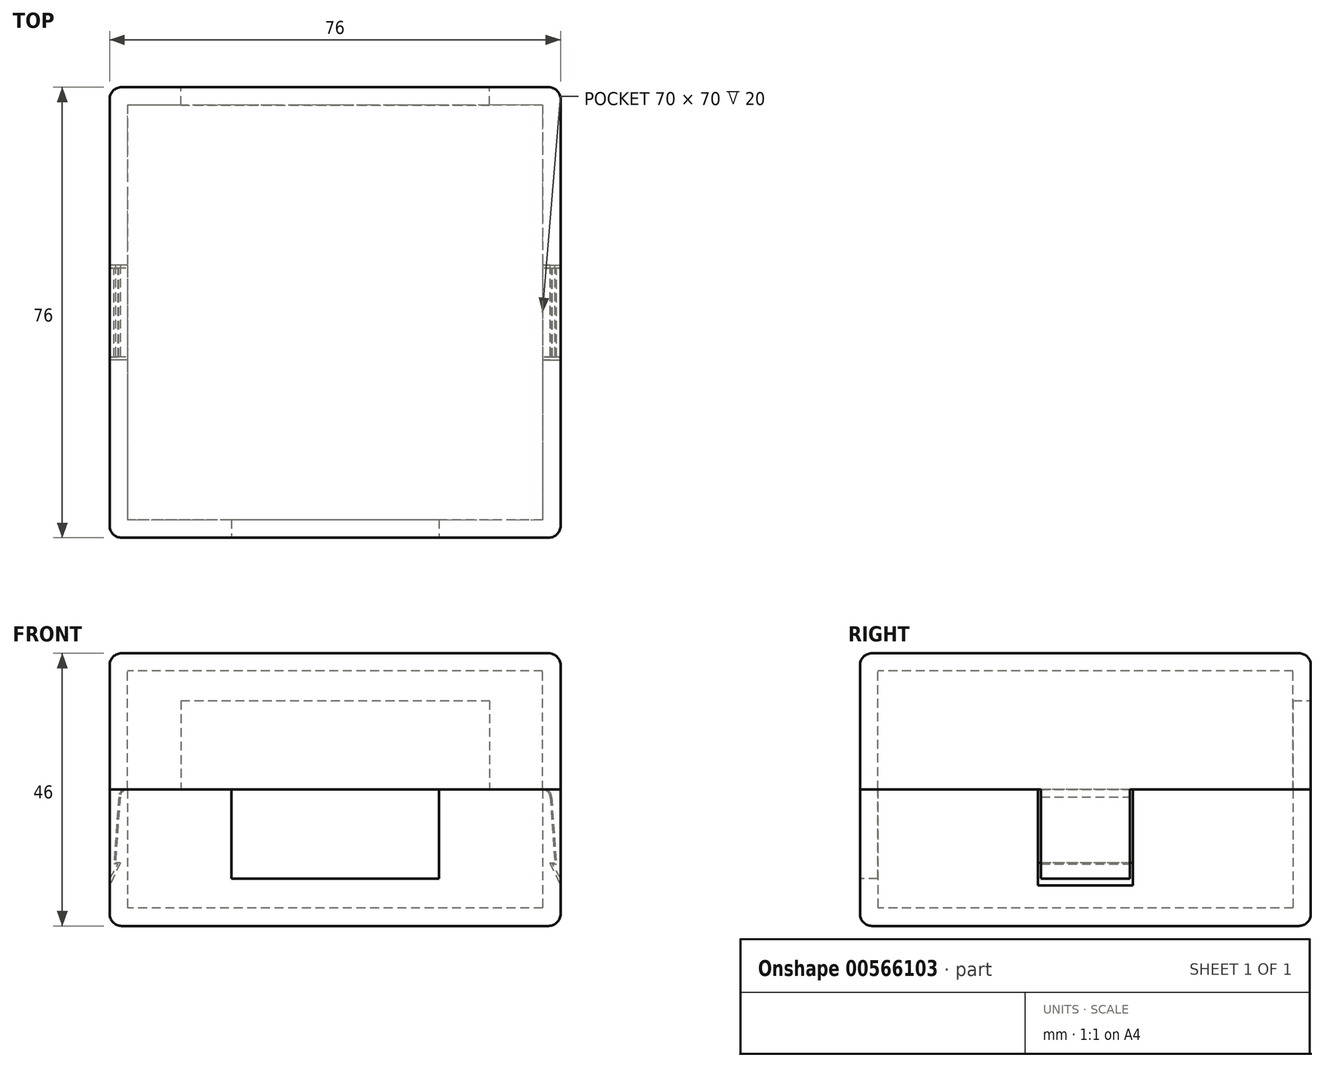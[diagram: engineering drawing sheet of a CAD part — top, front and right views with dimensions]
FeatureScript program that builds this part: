
annotation { "Feature Type Name" : "Feature", "Feature Type Description" : "" }
export const myFeature = defineFeature(function(context is Context, id is Id, definition is map)
    precondition{}
    {
        {
            var Q0;
            Q0=qCreatedBy(makeId("Top.planeOp"),FACE);
            var sketch = newSketch(context, id + "F0", { "sketchPlane" : qUnion([Q0])});
            skLineSegment(sketch, "E0.bottom", {"start": v(35, 35) * mm, "end": v(-35, 35) * mm});
            skLineSegment(sketch, "E0.top", {"start": v(35, -35) * mm, "end": v(-35, -35) * mm});
            skLineSegment(sketch, "E0.left", {"start": v(35, 35) * mm, "end": v(35, -35) * mm});
            skLineSegment(sketch, "E0.right", {"start": v(-35, 35) * mm, "end": v(-35, -35) * mm});
            skPoint(sketch, "E0.middle", {"position": v(0, 0) * mm});
            skLineSegment(sketch, "E1.0", {"start": v(38, 38) * mm, "end": v(-38, 38) * mm});
            skLineSegment(sketch, "E1.1", {"start": v(38, 38) * mm, "end": v(38, -38) * mm});
            skLineSegment(sketch, "E1.2", {"start": v(38, -38) * mm, "end": v(-38, -38) * mm});
            skLineSegment(sketch, "E1.3", {"start": v(-38, 38) * mm, "end": v(-38, -38) * mm});
            skSolve(sketch);
        }
        {
            var Q0;
            Q0=makeQuery(id+"F0.imprint","IMPRINT",FACE,{"disambiguationData":[TD([[makeQuery(id+"F0.imprint","IMPRINT",EDGE,{"derivedFrom":sQuery(id+"F0.wireOp",EDGE,"E0.bottom")}),-1.0]])]});
            var Q1;
            Q1=makeQuery(id+"F0.imprint","IMPRINT",FACE,{"disambiguationData":[TD([[makeQuery(id+"F0.imprint","IMPRINT",EDGE,{"derivedFrom":sQuery(id+"F0.wireOp",EDGE,"E0.bottom")}),1.0]])]});
            extrude(context, id + "F1", {"entities" : qUnion([Q0, Q1]), "oppositeDirection" : true, "depth" : 3 * mm, "offsetDistance" : 25 * mm});
        }
        {
            var Q0;
            Q0=makeQuery(id+"F0.imprint","IMPRINT",FACE,{"disambiguationData":[TD([[makeQuery(id+"F0.imprint","IMPRINT",EDGE,{"derivedFrom":sQuery(id+"F0.wireOp",EDGE,"E0.bottom")}),-1.0]])]});
            extrude(context, id + "F2", {"entities" : qUnion([Q0]), "operationType" : NewBodyOperationType.ADD, "depth" : 20 * mm, "offsetDistance" : 25 * mm});
        }
        {
            var Q0;
            Q0=makeQuery(id+"F1.opExtrude","SWEPT_BODY",BODY,{"disambiguationData":[OSD([sQuery(id+"F0.wireOp",EDGE,"E1.0"),sQuery(id+"F0.wireOp",EDGE,"E1.1"),sQuery(id+"F0.wireOp",EDGE,"E1.2"),sQuery(id+"F0.wireOp",EDGE,"E1.3")])]});
            var Q1;
            Q1=makeQuery(id+"F2.opExtrude","CAP_FACE",FACE,{"disambiguationData":[OSD([sQuery(id+"F0.wireOp",EDGE,"E0.bottom"),sQuery(id+"F0.wireOp",EDGE,"E0.top"),sQuery(id+"F0.wireOp",EDGE,"E0.left"),sQuery(id+"F0.wireOp",EDGE,"E0.right"),sQuery(id+"F0.wireOp",EDGE,"E1.0"),sQuery(id+"F0.wireOp",EDGE,"E1.1"),sQuery(id+"F0.wireOp",EDGE,"E1.2"),sQuery(id+"F0.wireOp",EDGE,"E1.3")])],"isStart":false});
            mirror(context, id + "F3", {"entities" : qUnion([Q0]), "mirrorPlane" : qUnion([Q1])});
        }
        {
            var Q0;
            {var subQ0=sQuery(id+"F0.wireOp",EDGE,"E1.2");Q0=makeQuery(id+"F3.opPattern","COPY",FACE,{"derivedFrom":makeQuery(id+"F2.boolean.opBoolean","MERGE",FACE,{"derivedFrom":[makeQuery(id+"F1.opExtrude","SWEPT_FACE",FACE,{"disambiguationData":[OSD([subQ0])]}),makeQuery(id+"F2.opExtrude","SWEPT_FACE",FACE,{"disambiguationData":[OSD([subQ0])]})]}),"instanceName":"1"});}
            var sketch = newSketch(context, id + "F4", { "sketchPlane" : qUnion([Q0])});
            skLineSegment(sketch, "E2.bottom", {"start": v(-17.5, 20) * mm, "end": v(17.5, 20) * mm});
            skLineSegment(sketch, "E2.top", {"start": v(-17.5, 5) * mm, "end": v(17.5, 5) * mm});
            skLineSegment(sketch, "E2.left", {"start": v(-17.5, 20) * mm, "end": v(-17.5, 5) * mm});
            skLineSegment(sketch, "E2.right", {"start": v(17.5, 20) * mm, "end": v(17.5, 5) * mm});
            skPoint(sketch, "E2.middle", {"position": v(0, 12.5) * mm});
            skSolve(sketch);
        }
        {
            var Q0;
            Q0=makeQuery(id+"F4.imprint","IMPRINT",FACE,{"disambiguationData":[TD([[makeQuery(id+"F4.imprint","IMPRINT",EDGE,{"derivedFrom":sQuery(id+"F4.wireOp",EDGE,"E2.bottom")}),1.0]])]});
            extrude(context, id + "F5", {"entities" : qUnion([Q0]), "operationType" : NewBodyOperationType.REMOVE, "endBound" : BoundingType.UP_TO_NEXT, "oppositeDirection" : true, "depth" : 25 * mm, "offsetDistance" : 25 * mm});
        }
        {
            var Q0;
            {var subQ0=sQuery(id+"F0.wireOp",EDGE,"E1.0");Q0=makeQuery(id+"F3.opPattern","COPY",FACE,{"derivedFrom":makeQuery(id+"F2.boolean.opBoolean","MERGE",FACE,{"derivedFrom":[makeQuery(id+"F1.opExtrude","SWEPT_FACE",FACE,{"disambiguationData":[OSD([subQ0])]}),makeQuery(id+"F2.opExtrude","SWEPT_FACE",FACE,{"disambiguationData":[OSD([subQ0])]})]}),"instanceName":"1"});}
            var sketch = newSketch(context, id + "F6", { "sketchPlane" : qUnion([Q0])});
            skLineSegment(sketch, "E3.bottom", {"start": v(26, 35) * mm, "end": v(-26, 35) * mm});
            skLineSegment(sketch, "E3.top", {"start": v(26, 20) * mm, "end": v(-26, 20) * mm});
            skLineSegment(sketch, "E3.left", {"start": v(26, 35) * mm, "end": v(26, 20) * mm});
            skLineSegment(sketch, "E3.right", {"start": v(-26, 35) * mm, "end": v(-26, 20) * mm});
            skPoint(sketch, "E3.middle", {"position": v(0, 27.5) * mm});
            skSolve(sketch);
        }
        {
            var Q0;
            Q0=makeQuery(id+"F6.imprint","IMPRINT",FACE,{"disambiguationData":[TD([[makeQuery(id+"F6.imprint","IMPRINT",EDGE,{"derivedFrom":sQuery(id+"F6.wireOp",EDGE,"E3.bottom")}),1.0]])]});
            extrude(context, id + "F7", {"entities" : qUnion([Q0]), "operationType" : NewBodyOperationType.REMOVE, "endBound" : BoundingType.UP_TO_NEXT, "oppositeDirection" : true, "depth" : 25 * mm, "offsetDistance" : 25 * mm});
        }
        {
            var Q0;
            Q0=qCreatedBy(makeId("Front.planeOp"),FACE);
            var sketch = newSketch(context, id + "F8", { "sketchPlane" : qUnion([Q0])});
            skLineSegment(sketch, "E4.0", {"start": v(38, 43) * mm, "end": v(38, 20) * mm});
            skLineSegment(sketch, "E5", {"start": v(38, 20) * mm, "end": v(38, 5) * mm});
            skLineSegment(sketch, "E6", {"start": v(38, 5) * mm, "end": v(36.6, 7.42) * mm});
            skLineSegment(sketch, "E7", {"start": v(36.6, 7.42) * mm, "end": v(37.3, 7.42) * mm});
            skLineSegment(sketch, "E8", {"start": v(36.4, 20) * mm, "end": v(38, 20) * mm});
            skLineSegment(sketch, "E9.0", {"start": v(38, 20) * mm, "end": v(-38, 20) * mm});
            skArc(sketch, "E10", {"start": v(36.49, 18.76) * mm, "mid": v(36.13, 19.64) * mm, "end": v(35.25, 20) * mm});
            skLineSegment(sketch, "E11", {"start": v(35.25, 20) * mm, "end": v(36.4, 20) * mm});
            skLineSegment(sketch, "E12", {"start": v(36.49, 18.76) * mm, "end": v(37.3, 7.42) * mm});
            skLineSegment(sketch, "E13", {"start": v(36.49, 18.76) * mm, "end": v(36.4, 20) * mm, "construction": true});
            skLineSegment(sketch, "E14.0", {"start": v(36.24, 18.76) * mm, "end": v(37.03, 7.67) * mm});
            skLineSegment(sketch, "E14.1", {"start": v(36.2, 7.67) * mm, "end": v(37.03, 7.67) * mm});
            skArc(sketch, "E15", {"start": v(36.24, 18.76) * mm, "mid": v(35.85, 19.61) * mm, "end": v(35, 20) * mm});
            skLineSegment(sketch, "E16", {"start": v(36.2, 7.67) * mm, "end": v(38, 3.81) * mm});
            skLineSegment(sketch, "E17.MirrorCS", {"start": v(-36.6, 7.42) * mm, "end": v(-37.3, 7.42) * mm});
            skLineSegment(sketch, "E18.MirrorCS", {"start": v(-38, 5) * mm, "end": v(-36.6, 7.42) * mm});
            skLineSegment(sketch, "E19.MirrorCS", {"start": v(-36.2, 7.67) * mm, "end": v(-38, 3.81) * mm});
            skLineSegment(sketch, "E20.MirrorCS", {"start": v(-36.2, 7.67) * mm, "end": v(-37.03, 7.67) * mm});
            skLineSegment(sketch, "E21.MirrorCS", {"start": v(-36.24, 18.76) * mm, "end": v(-37.03, 7.67) * mm});
            skLineSegment(sketch, "E22.MirrorCS", {"start": v(-36.49, 18.76) * mm, "end": v(-37.3, 7.42) * mm});
            skArc(sketch, "E23.MirrorCS", {"start": v(-36.49, 18.76) * mm, "mid": v(-36.13, 19.64) * mm, "end": v(-35.25, 20) * mm});
            skArc(sketch, "E24.MirrorCS", {"start": v(-36.24, 18.76) * mm, "mid": v(-35.85, 19.61) * mm, "end": v(-35, 20) * mm});
            skLineSegment(sketch, "E25", {"start": v(-38, 20) * mm, "end": v(-38, 3.81) * mm});
            skLineSegment(sketch, "E26", {"start": v(38, 5) * mm, "end": v(38, 3.81) * mm});
            skSolve(sketch);
        }
        {
            var Q0;
            Q0=makeQuery(id+"F8.imprint","IMPRINT",FACE,{"disambiguationData":[TD([[makeQuery(id+"F8.imprint","IMPRINT",EDGE,{"derivedFrom":sQuery(id+"F8.wireOp",EDGE,"E17.MirrorCS")}),-1.0]])]});
            var Q1;
            Q1=makeQuery(id+"F8.imprint","IMPRINT",FACE,{"disambiguationData":[TD([[makeQuery(id+"F8.imprint","IMPRINT",EDGE,{"derivedFrom":sQuery(id+"F8.wireOp",EDGE,"E17.MirrorCS")}),1.0]])]});
            var Q2;
            {var subQ1=sQuery(id+"F8.wireOp",EDGE,"E5");Q2=makeQuery(id+"F8.imprint","IMPRINT",FACE,{"disambiguationData":[TD([[makeQuery(id+"F8.imprint","IMPRINT",EDGE,{"derivedFrom":subQ1}),-1.0]])]});}
            var Q3;
            Q3=makeQuery(id+"F8.imprint","IMPRINT",FACE,{"disambiguationData":[TD([[makeQuery(id+"F8.imprint","IMPRINT",EDGE,{"derivedFrom":sQuery(id+"F8.wireOp",EDGE,"E6")}),1.0]])]});
            extrude(context, id + "F9", {"entities" : qUnion([Q0, Q1, Q2, Q3]), "operationType" : NewBodyOperationType.REMOVE, "endBound" : BoundingType.SYMMETRIC, "oppositeDirection" : true, "depth" : 16 * mm, "offsetDistance" : 25 * mm});
        }
        {
            var Q0;
            Q0=makeQuery(id+"F8.imprint","IMPRINT",FACE,{"disambiguationData":[TD([[makeQuery(id+"F8.imprint","IMPRINT",EDGE,{"derivedFrom":sQuery(id+"F8.wireOp",EDGE,"E17.MirrorCS")}),1.0]])]});
            var Q1;
            {var subQ1=sQuery(id+"F8.wireOp",EDGE,"E5");Q1=makeQuery(id+"F8.imprint","IMPRINT",FACE,{"disambiguationData":[TD([[makeQuery(id+"F8.imprint","IMPRINT",EDGE,{"derivedFrom":subQ1}),-1.0]])]});}
            extrude(context, id + "F10", {"entities" : qUnion([Q0, Q1]), "operationType" : NewBodyOperationType.ADD, "endBound" : BoundingType.SYMMETRIC, "depth" : 15 * mm, "offsetDistance" : 25 * mm});
        }
        {
            var Q0;
            {var subQ0=sQuery(id+"F0.wireOp",EDGE,"E1.3");var subQ1=sQuery(id+"F0.wireOp",EDGE,"E1.2");Q0=makeQuery(id+"F3.opPattern","COPY",EDGE,{"derivedFrom":makeQuery(id+"F2.boolean.opBoolean","MERGE",EDGE,{"derivedFrom":[makeQuery(id+"F1.opExtrude","SWEPT_EDGE",EDGE,{"disambiguationData":[OSD([subQ1,subQ0])]}),makeQuery(id+"F2.opExtrude","SWEPT_EDGE",EDGE,{"disambiguationData":[OSD([subQ1,subQ0])]})]}),"instanceName":"1"});}
            var Q1;
            {var subQ0=sQuery(id+"F0.wireOp",EDGE,"E1.3");var subQ1=sQuery(id+"F0.wireOp",EDGE,"E1.2");Q1=makeQuery(id+"F2.boolean.opBoolean","MERGE",EDGE,{"derivedFrom":[makeQuery(id+"F1.opExtrude","SWEPT_EDGE",EDGE,{"disambiguationData":[OSD([subQ1,subQ0])]}),makeQuery(id+"F2.opExtrude","SWEPT_EDGE",EDGE,{"disambiguationData":[OSD([subQ1,subQ0])]})]});}
            var Q2;
            Q2=makeQuery(id+"F1.opExtrude","CAP_EDGE",EDGE,{"disambiguationData":[OSD([sQuery(id+"F0.wireOp",EDGE,"E1.2")])],"isStart":false});
            var Q3;
            Q3=makeQuery(id+"F1.opExtrude","CAP_EDGE",EDGE,{"disambiguationData":[OSD([sQuery(id+"F0.wireOp",EDGE,"E1.3")])],"isStart":false});
            var Q4;
            Q4=makeQuery(id+"F3.opPattern","COPY",EDGE,{"derivedFrom":makeQuery(id+"F1.opExtrude","CAP_EDGE",EDGE,{"disambiguationData":[OSD([sQuery(id+"F0.wireOp",EDGE,"E1.2")])],"isStart":false}),"instanceName":"1"});
            var Q5;
            Q5=makeQuery(id+"F3.opPattern","COPY",EDGE,{"derivedFrom":makeQuery(id+"F1.opExtrude","CAP_EDGE",EDGE,{"disambiguationData":[OSD([sQuery(id+"F0.wireOp",EDGE,"E1.3")])],"isStart":false}),"instanceName":"1"});
            var Q6;
            {var subQ0=sQuery(id+"F0.wireOp",EDGE,"E1.3");var subQ1=sQuery(id+"F0.wireOp",EDGE,"E1.0");Q6=makeQuery(id+"F2.boolean.opBoolean","MERGE",EDGE,{"derivedFrom":[makeQuery(id+"F1.opExtrude","SWEPT_EDGE",EDGE,{"disambiguationData":[OSD([subQ1,subQ0])]}),makeQuery(id+"F2.opExtrude","SWEPT_EDGE",EDGE,{"disambiguationData":[OSD([subQ1,subQ0])]})]});}
            var Q7;
            {var subQ0=sQuery(id+"F0.wireOp",EDGE,"E1.3");var subQ1=sQuery(id+"F0.wireOp",EDGE,"E1.0");Q7=makeQuery(id+"F3.opPattern","COPY",EDGE,{"derivedFrom":makeQuery(id+"F2.boolean.opBoolean","MERGE",EDGE,{"derivedFrom":[makeQuery(id+"F1.opExtrude","SWEPT_EDGE",EDGE,{"disambiguationData":[OSD([subQ1,subQ0])]}),makeQuery(id+"F2.opExtrude","SWEPT_EDGE",EDGE,{"disambiguationData":[OSD([subQ1,subQ0])]})]}),"instanceName":"1"});}
            var Q8;
            Q8=makeQuery(id+"F3.opPattern","COPY",EDGE,{"derivedFrom":makeQuery(id+"F1.opExtrude","CAP_EDGE",EDGE,{"disambiguationData":[OSD([sQuery(id+"F0.wireOp",EDGE,"E1.0")])],"isStart":false}),"instanceName":"1"});
            var Q9;
            Q9=makeQuery(id+"F1.opExtrude","CAP_EDGE",EDGE,{"disambiguationData":[OSD([sQuery(id+"F0.wireOp",EDGE,"E1.0")])],"isStart":false});
            var Q10;
            {var subQ0=sQuery(id+"F0.wireOp",EDGE,"E1.1");var subQ1=sQuery(id+"F0.wireOp",EDGE,"E1.0");Q10=makeQuery(id+"F2.boolean.opBoolean","MERGE",EDGE,{"derivedFrom":[makeQuery(id+"F1.opExtrude","SWEPT_EDGE",EDGE,{"disambiguationData":[OSD([subQ1,subQ0])]}),makeQuery(id+"F2.opExtrude","SWEPT_EDGE",EDGE,{"disambiguationData":[OSD([subQ1,subQ0])]})]});}
            var Q11;
            {var subQ0=sQuery(id+"F0.wireOp",EDGE,"E1.1");var subQ1=sQuery(id+"F0.wireOp",EDGE,"E1.0");Q11=makeQuery(id+"F3.opPattern","COPY",EDGE,{"derivedFrom":makeQuery(id+"F2.boolean.opBoolean","MERGE",EDGE,{"derivedFrom":[makeQuery(id+"F1.opExtrude","SWEPT_EDGE",EDGE,{"disambiguationData":[OSD([subQ1,subQ0])]}),makeQuery(id+"F2.opExtrude","SWEPT_EDGE",EDGE,{"disambiguationData":[OSD([subQ1,subQ0])]})]}),"instanceName":"1"});}
            var Q12;
            Q12=makeQuery(id+"F1.opExtrude","CAP_EDGE",EDGE,{"disambiguationData":[OSD([sQuery(id+"F0.wireOp",EDGE,"E1.1")])],"isStart":false});
            var Q13;
            Q13=makeQuery(id+"F3.opPattern","COPY",EDGE,{"derivedFrom":makeQuery(id+"F1.opExtrude","CAP_EDGE",EDGE,{"disambiguationData":[OSD([sQuery(id+"F0.wireOp",EDGE,"E1.1")])],"isStart":false}),"instanceName":"1"});
            var Q14;
            {var subQ0=sQuery(id+"F0.wireOp",EDGE,"E1.2");var subQ1=sQuery(id+"F0.wireOp",EDGE,"E1.1");Q14=makeQuery(id+"F3.opPattern","COPY",EDGE,{"derivedFrom":makeQuery(id+"F2.boolean.opBoolean","MERGE",EDGE,{"derivedFrom":[makeQuery(id+"F1.opExtrude","SWEPT_EDGE",EDGE,{"disambiguationData":[OSD([subQ1,subQ0])]}),makeQuery(id+"F2.opExtrude","SWEPT_EDGE",EDGE,{"disambiguationData":[OSD([subQ1,subQ0])]})]}),"instanceName":"1"});}
            var Q15;
            {var subQ0=sQuery(id+"F0.wireOp",EDGE,"E1.2");var subQ1=sQuery(id+"F0.wireOp",EDGE,"E1.1");Q15=makeQuery(id+"F2.boolean.opBoolean","MERGE",EDGE,{"derivedFrom":[makeQuery(id+"F1.opExtrude","SWEPT_EDGE",EDGE,{"disambiguationData":[OSD([subQ1,subQ0])]}),makeQuery(id+"F2.opExtrude","SWEPT_EDGE",EDGE,{"disambiguationData":[OSD([subQ1,subQ0])]})]});}
            fillet(context, id + "F11", {"entities" : qUnion([Q0, Q1, Q2, Q3, Q4, Q5, Q6, Q7, Q8, Q9, Q10, Q11, Q12, Q13, Q14, Q15]), "radius" : 2 * mm, "tangentPropagation" : true, "allowEdgeOverflow" : false});
        }
    });
